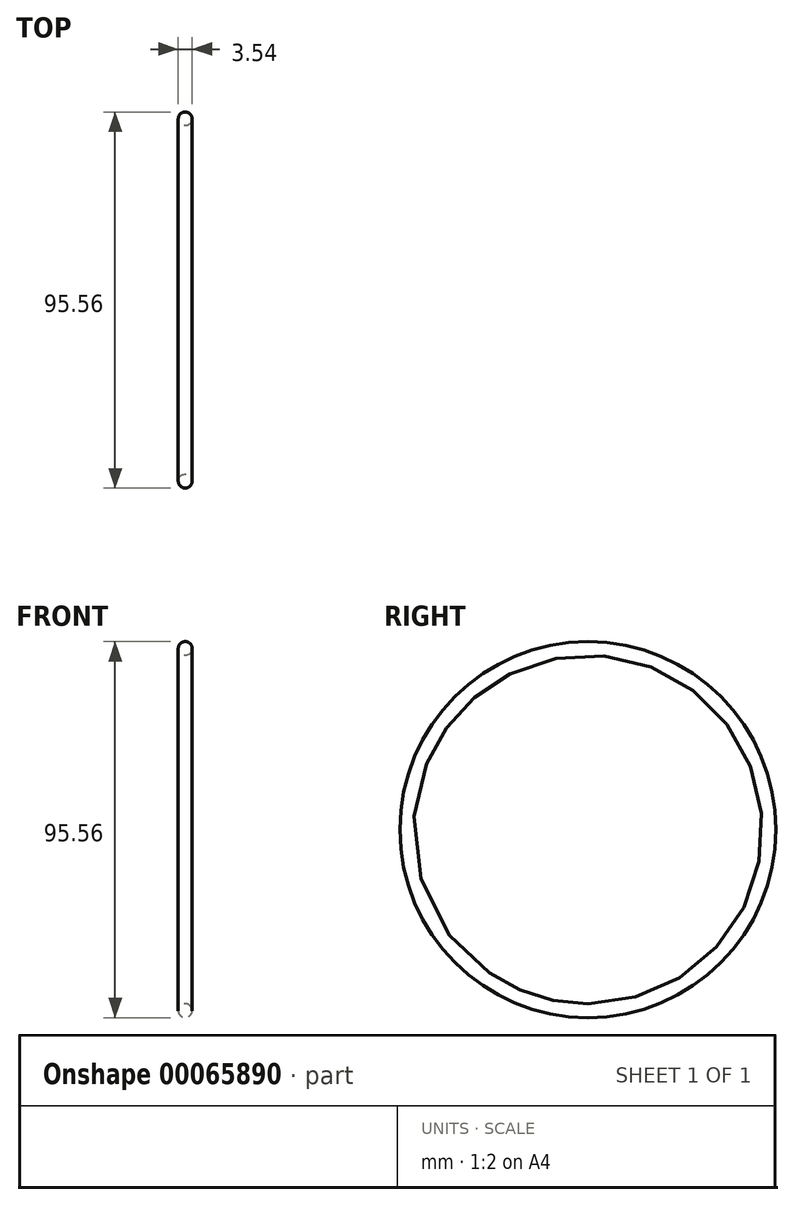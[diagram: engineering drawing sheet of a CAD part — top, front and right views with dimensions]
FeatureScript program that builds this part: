
annotation { "Feature Type Name" : "Feature", "Feature Type Description" : "" }
export const myFeature = defineFeature(function(context is Context, id is Id, definition is map)
    precondition{}
    {
        {
            var Q0;
            Q0=qCreatedBy(makeId("Front.planeOp"),FACE);
            var sketch = newSketch(context, id + "F0", { "sketchPlane" : qUnion([Q0])});
            skLineSegment(sketch, "E0", {"start": v(0, 0) * mm, "end": v(-6.06, 0) * mm, "construction": true});
            skCircle(sketch, "E1", {"center": v(0, 46.01) * mm, "radius": 1.77 * mm});
            skSolve(sketch);
        }
        {
            var Q0;
            Q0=makeQuery(id+"F0.imprint","IMPRINT",FACE,{"disambiguationData":[TD([[makeQuery(id+"F0.imprint","IMPRINT",EDGE,{"derivedFrom":sQuery(id+"F0.wireOp",EDGE,"E1")}),1.0]])]});
            var Q1;
            Q1=sQuery(id+"F0.wireOp",EDGE,"E0");
            revolve(context, id + "F1", {"entities" : qUnion([Q0]), "axis" : qUnion([Q1]), "revolveType" : RevolveType.FULL});
        }
    });
